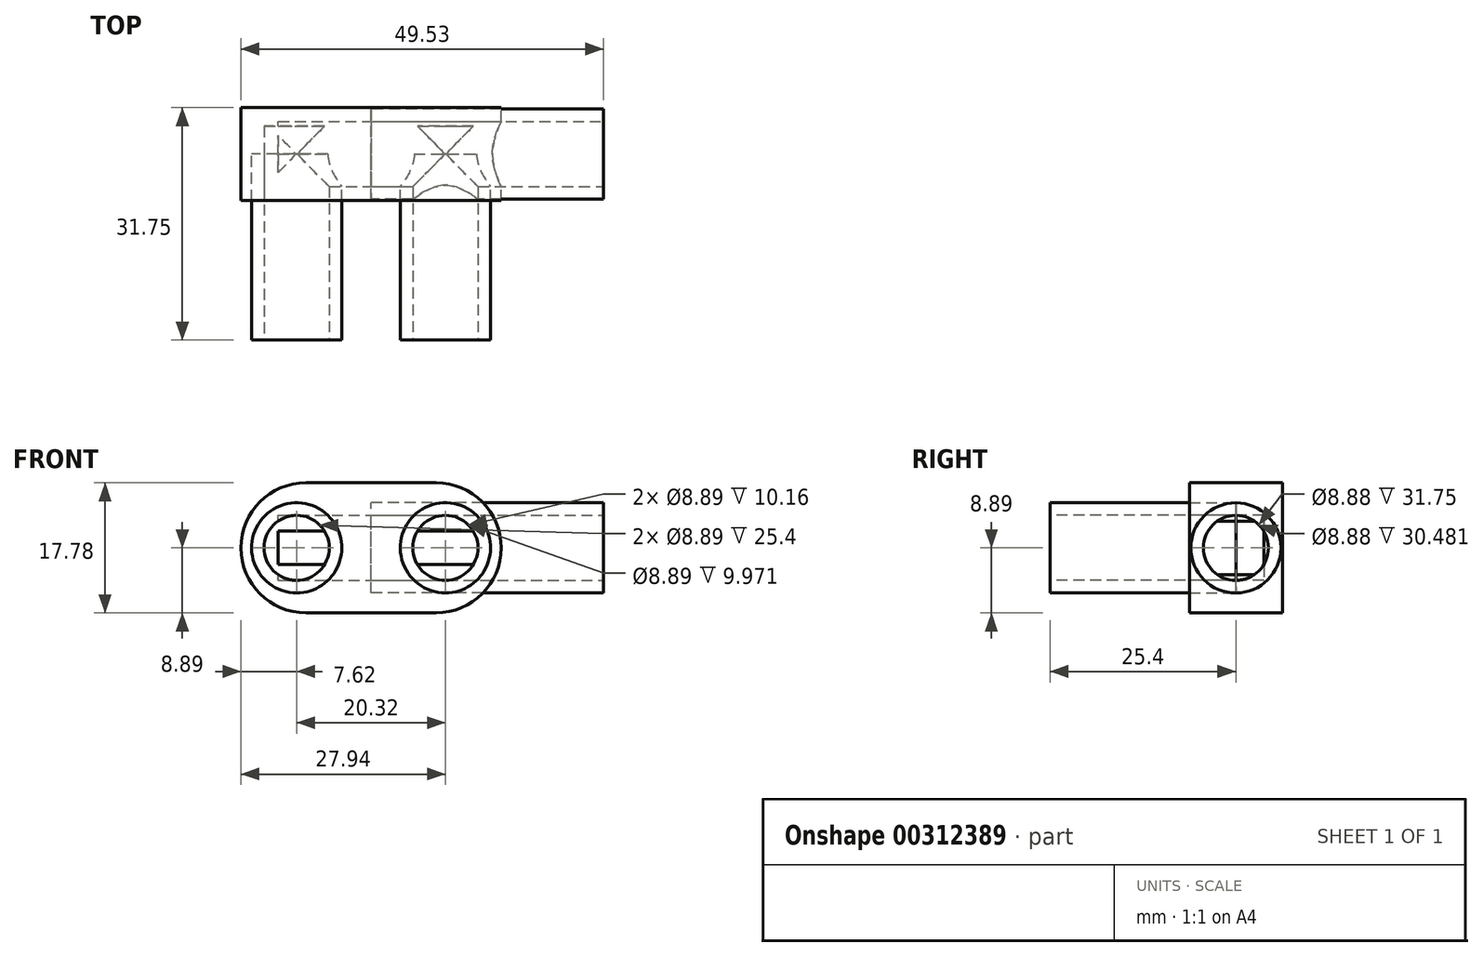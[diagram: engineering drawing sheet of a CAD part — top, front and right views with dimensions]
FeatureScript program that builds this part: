
annotation { "Feature Type Name" : "Feature", "Feature Type Description" : "" }
export const myFeature = defineFeature(function(context is Context, id is Id, definition is map)
    precondition{}
    {
        {
            var Q0;
            Q0=qCreatedBy(makeId("Front.planeOp"),FACE);
            var sketch = newSketch(context, id + "F0", { "sketchPlane" : qUnion([Q0])});
            skCircle(sketch, "E0", {"center": v(10.16, 0) * mm, "radius": 6.16 * mm});
            skCircle(sketch, "E1.MirrorC", {"center": v(-10.16, 0) * mm, "radius": 6.16 * mm});
            skSolve(sketch);
        }
        {
            var Q0;
            Q0 = qSketchRegion(id + "F0", true);
            extrude(context, id + "F1", {"entities" : qUnion([Q0]), "depth" : 25.4 * mm});
        }
        {
            var Q0;
            Q0=qCreatedBy(makeId("Front.planeOp"),FACE);
            var sketch = newSketch(context, id + "F2", { "sketchPlane" : qUnion([Q0])});
            skArc(sketch, "E2.MirrorC", {"start": v(-8.89, -8.9) * mm, "mid": v(-17.78, 0) * mm, "end": v(-8.9, 8.9) * mm});
            skLineSegment(sketch, "E3", {"start": v(8.9, 8.9) * mm, "end": v(-8.9, 8.9) * mm});
            skLineSegment(sketch, "E4.MirrorCS", {"start": v(8.9, -8.9) * mm, "end": v(-8.9, -8.9) * mm});
            skPoint(sketch, "E5.0.center.orphan", {"position": v(8.9, 0) * mm});
            skArc(sketch, "E6.MirrorCS", {"start": v(8.89, -8.9) * mm, "mid": v(17.78, 0) * mm, "end": v(8.9, 8.9) * mm});
            skSolve(sketch);
        }
        {
            var Q0;
            Q0 = qSketchRegion(id + "F2", true);
            extrude(context, id + "F3", {"entities" : qUnion([Q0]), "endBound" : BoundingType.SYMMETRIC, "depth" : 12.7 * mm});
        }
        {
            var Q0;
            Q0=qCreatedBy(makeId("Right.planeOp"),FACE);
            var sketch = newSketch(context, id + "F4", { "sketchPlane" : qUnion([Q0])});
            skCircle(sketch, "E7", {"center": v(0, 0) * mm, "radius": 6.16 * mm});
            skSolve(sketch);
        }
        {
            var Q0;
            Q0 = qSketchRegion(id + "F4", true);
            extrude(context, id + "F5", {"entities" : qUnion([Q0]), "depth" : 31.75 * mm});
        }
        {
            var Q0;
            Q0=makeQuery(id+"F5.opExtrude","CAP_FACE",FACE,{"disambiguationData":[OSD([sQuery(id+"F4.wireOp",EDGE,"E7")])],"isStart":false});
            var sketch = newSketch(context, id + "F6", { "sketchPlane" : qUnion([Q0])});
            skCircle(sketch, "E8", {"center": v(0, 0) * mm, "radius": 4.44 * mm});
            skSolve(sketch);
        }
        {
            var Q0;
            Q0=makeQuery(id+"F6.imprint","IMPRINT",FACE,{"disambiguationData":[TD([[makeQuery(id+"F6.imprint","IMPRINT",EDGE,{"derivedFrom":sQuery(id+"F6.wireOp",EDGE,"E8")}),1.0]])]});
            var Q1;
            Q1=sQuery(id+"F6.wireOp",EDGE,"E8");
            extrude(context, id + "F7", {"entities" : qUnion([Q0]), "operationType" : NewBodyOperationType.REMOVE, "surfaceEntities" : qUnion([Q1]), "oppositeDirection" : true, "depth" : 44.45 * mm});
        }
        {
            var Q0;
            Q0=makeQuery(id+"F1.opExtrude","CAP_FACE",FACE,{"disambiguationData":[OSD([sQuery(id+"F0.wireOp",EDGE,"E1.MirrorC")])],"isStart":false});
            var sketch = newSketch(context, id + "F8", { "sketchPlane" : qUnion([Q0])});
            skCircle(sketch, "E9", {"center": v(-10.16, 0) * mm, "radius": 4.45 * mm});
            skCircle(sketch, "E10", {"center": v(10.16, 0) * mm, "radius": 4.45 * mm});
            skSolve(sketch);
        }
        {
            var Q0;
            Q0 = qSketchRegion(id + "F8", true);
            extrude(context, id + "F9", {"entities" : qUnion([Q0]), "operationType" : NewBodyOperationType.REMOVE, "oppositeDirection" : true, "depth" : 29.2 * mm});
        }
    });
